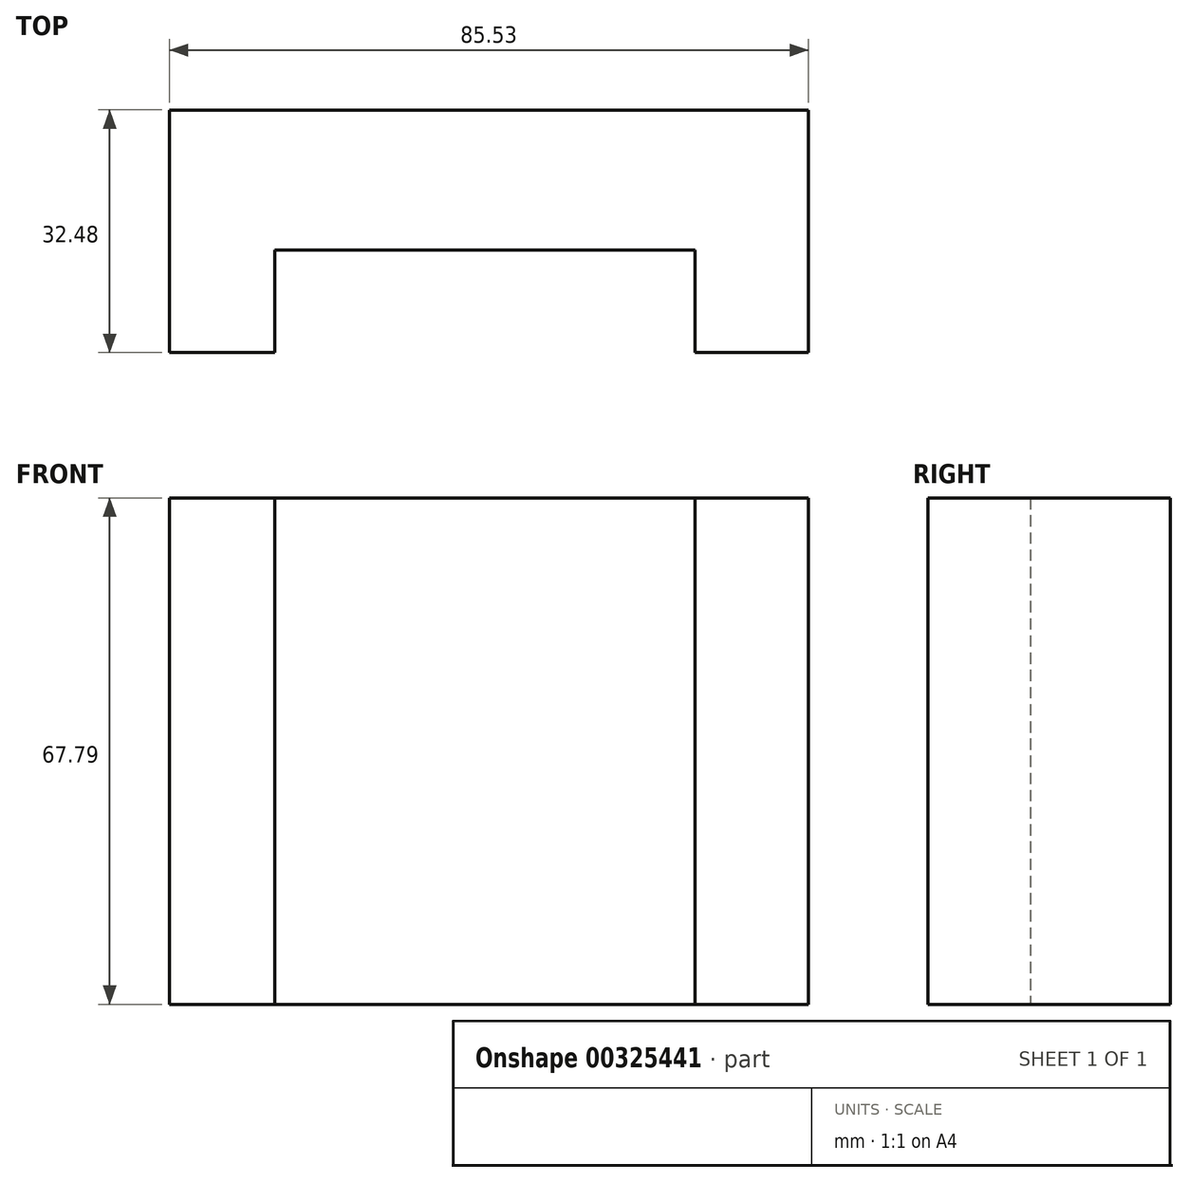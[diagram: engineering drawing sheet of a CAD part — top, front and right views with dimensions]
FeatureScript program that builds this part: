
annotation { "Feature Type Name" : "Feature", "Feature Type Description" : "" }
export const myFeature = defineFeature(function(context is Context, id is Id, definition is map)
    precondition{}
    {
        {
            var Q0;
            Q0=qCreatedBy(makeId("Top.planeOp"),FACE);
            var sketch = newSketch(context, id + "F0", { "sketchPlane" : qUnion([Q0])});
            skLineSegment(sketch, "E0.bottom", {"start": v(-35.37, 55.94) * mm, "end": v(50.16, 55.94) * mm});
            skLineSegment(sketch, "E0.top", {"start": v(-35.37, 23.46) * mm, "end": v(-21.3, 23.46) * mm});
            skLineSegment(sketch, "E0.left", {"start": v(-35.37, 55.94) * mm, "end": v(-35.37, 23.46) * mm});
            skLineSegment(sketch, "E0.right", {"start": v(50.16, 55.94) * mm, "end": v(50.16, 23.46) * mm});
            skLineSegment(sketch, "E1", {"start": v(-21.3, 23.46) * mm, "end": v(-21.3, 37.17) * mm});
            skLineSegment(sketch, "E2", {"start": v(-21.3, 37.17) * mm, "end": v(35, 37.17) * mm});
            skLineSegment(sketch, "E3", {"start": v(35, 37.17) * mm, "end": v(35, 23.46) * mm});
            skLineSegment(sketch, "E4.trimOffspring", {"start": v(35, 23.46) * mm, "end": v(50.16, 23.46) * mm});
            skSolve(sketch);
        }
        {
            var Q0;
            Q0 = qSketchRegion(id + "F0", true);
            extrude(context, id + "F1", {"entities" : qUnion([Q0]), "depth" : 67.8 * mm});
        }
    });
